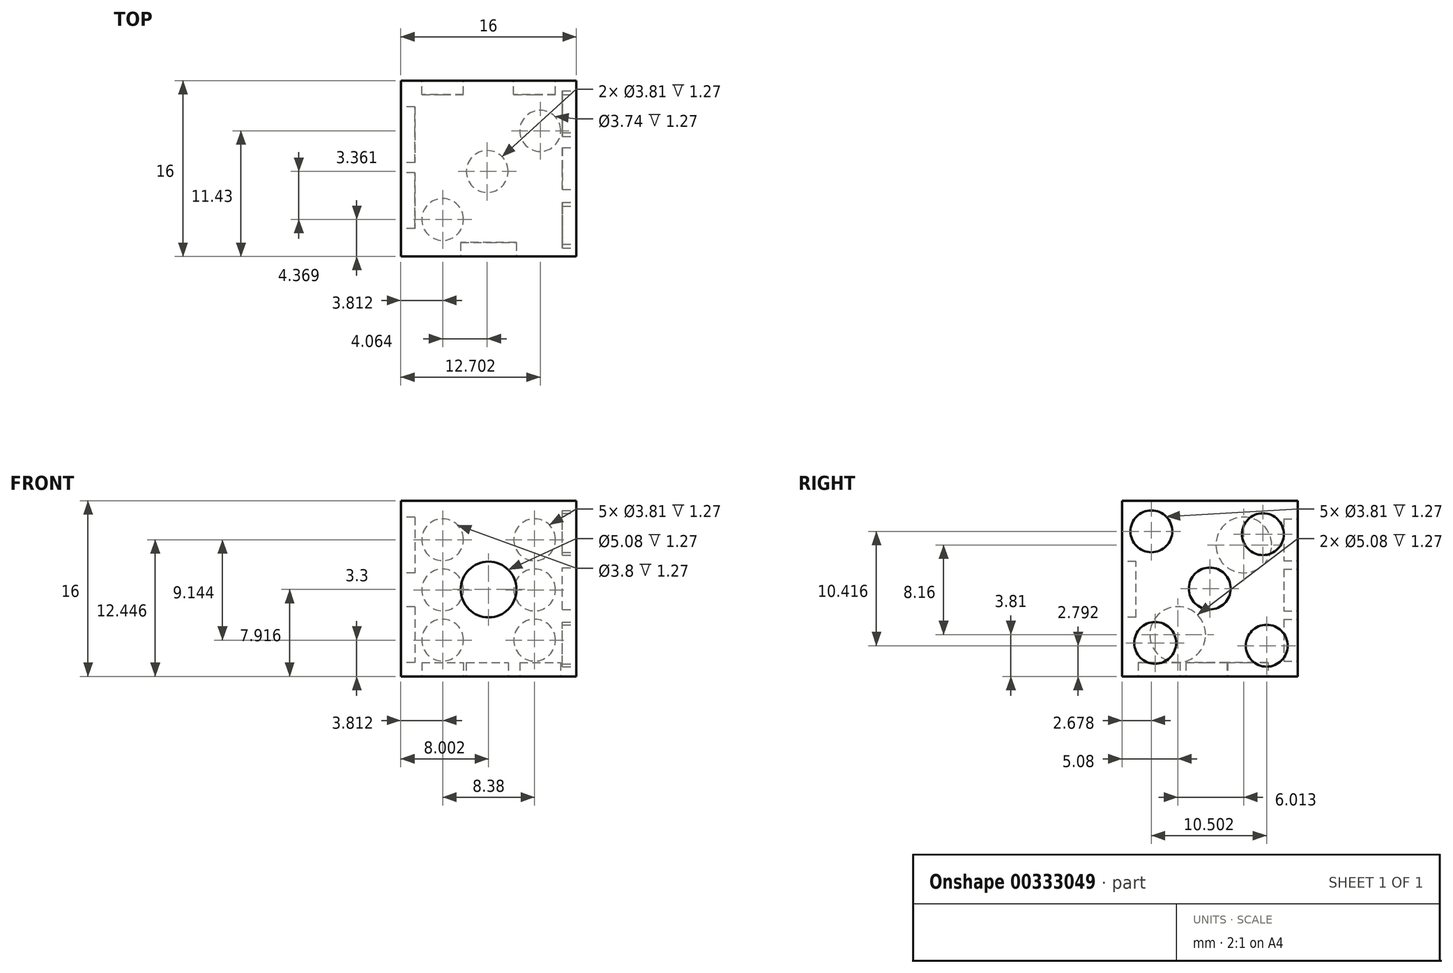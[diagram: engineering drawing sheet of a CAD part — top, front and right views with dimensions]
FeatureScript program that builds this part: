
annotation { "Feature Type Name" : "Feature", "Feature Type Description" : "" }
export const myFeature = defineFeature(function(context is Context, id is Id, definition is map)
    precondition{}
    {
        {
            var Q0;
            Q0=qCreatedBy(makeId("Front.planeOp"),FACE);
            var sketch = newSketch(context, id + "F0", { "sketchPlane" : qUnion([Q0])});
            skLineSegment(sketch, "E0.bottom", {"start": v(22.63, 56.48) * mm, "end": v(38.63, 56.48) * mm});
            skLineSegment(sketch, "E0.top", {"start": v(22.63, 40.48) * mm, "end": v(38.63, 40.48) * mm});
            skLineSegment(sketch, "E0.left", {"start": v(22.63, 56.48) * mm, "end": v(22.63, 40.48) * mm});
            skLineSegment(sketch, "E0.right", {"start": v(38.63, 56.48) * mm, "end": v(38.63, 40.48) * mm});
            skSolve(sketch);
        }
        {
            var Q0;
            Q0=makeQuery(id+"F0.imprint","IMPRINT",FACE,{"disambiguationData":[TD([[makeQuery(id+"F0.imprint","IMPRINT",EDGE,{"derivedFrom":sQuery(id+"F0.wireOp",EDGE,"E0.bottom")}),-1.0]])]});
            extrude(context, id + "F1", {"entities" : qUnion([Q0]), "oppositeDirection" : true, "depth" : 16 * mm});
        }
        {
            var Q0;
            Q0=makeQuery(id+"F1.opExtrude","CAP_FACE",FACE,{"disambiguationData":[OSD([sQuery(id+"F0.wireOp",EDGE,"E0.bottom"),sQuery(id+"F0.wireOp",EDGE,"E0.top"),sQuery(id+"F0.wireOp",EDGE,"E0.left"),sQuery(id+"F0.wireOp",EDGE,"E0.right")])],"isStart":true});
            var sketch = newSketch(context, id + "F2", { "sketchPlane" : qUnion([Q0])});
            skCircle(sketch, "E1", {"center": v(30.63, 48.4) * mm, "radius": 0.08 * mm});
            skPoint(sketch, "E1.centerSnap0", {"position": v(30.63, 40.48) * mm});
            skCircle(sketch, "E2", {"center": v(30.63, 48.4) * mm, "radius": 2.54 * mm});
            skSolve(sketch);
        }
        {
            var Q0;
            Q0=makeQuery(id+"F2.imprint","IMPRINT",FACE,{"disambiguationData":[TD([[makeQuery(id+"F2.imprint","IMPRINT",EDGE,{"derivedFrom":sQuery(id+"F2.wireOp",EDGE,"E1")}),-1.0]])]});
            extrude(context, id + "F3", {"entities" : qUnion([Q0]), "operationType" : NewBodyOperationType.REMOVE, "oppositeDirection" : true, "depth" : 1.27 * mm});
        }
        {
            var Q0;
            Q0=makeQuery(id+"F3.boolean.opBoolean","SPLIT",FACE,{"disambiguationData":[TD([makeQuery(id+"F3.opExtrude","SWEPT_FACE",FACE,{"disambiguationData":[OSD([sQuery(id+"F2.wireOp",EDGE,"E1")])]})])],"derivedFrom":makeQuery(id+"F1.opExtrude","CAP_FACE",FACE,{"disambiguationData":[OSD([sQuery(id+"F0.wireOp",EDGE,"E0.bottom"),sQuery(id+"F0.wireOp",EDGE,"E0.top"),sQuery(id+"F0.wireOp",EDGE,"E0.left"),sQuery(id+"F0.wireOp",EDGE,"E0.right")])],"isStart":true})});
            extrude(context, id + "F4", {"entities" : qUnion([Q0]), "operationType" : NewBodyOperationType.REMOVE, "oppositeDirection" : true, "depth" : 1.27 * mm});
        }
        {
            var Q0;
            Q0=makeQuery(id+"F1.opExtrude","SWEPT_FACE",FACE,{"disambiguationData":[OSD([sQuery(id+"F0.wireOp",EDGE,"E0.left")])]});
            var sketch = newSketch(context, id + "F5", { "sketchPlane" : qUnion([Q0])});
            skCircle(sketch, "E3", {"center": v(-11.1, 52.45) * mm, "radius": 2.54 * mm});
            skCircle(sketch, "E4", {"center": v(-5.08, 44.3) * mm, "radius": 2.54 * mm});
            skSolve(sketch);
        }
        {
            var Q0;
            Q0=makeQuery(id+"F5.imprint","IMPRINT",FACE,{"disambiguationData":[TD([[makeQuery(id+"F5.imprint","IMPRINT",EDGE,{"derivedFrom":sQuery(id+"F5.wireOp",EDGE,"E3")}),1.0]])]});
            extrude(context, id + "F6", {"entities" : qUnion([Q0]), "operationType" : NewBodyOperationType.REMOVE, "oppositeDirection" : true, "depth" : 1.27 * mm});
        }
        {
            var Q0;
            Q0 = qSketchRegion(id + "F5", true);
            extrude(context, id + "F7", {"entities" : qUnion([Q0]), "operationType" : NewBodyOperationType.REMOVE, "oppositeDirection" : true, "depth" : 1.27 * mm});
        }
        {
            var Q0;
            Q0=makeQuery(id+"F1.opExtrude","CAP_FACE",FACE,{"disambiguationData":[OSD([sQuery(id+"F0.wireOp",EDGE,"E0.bottom"),sQuery(id+"F0.wireOp",EDGE,"E0.top"),sQuery(id+"F0.wireOp",EDGE,"E0.left"),sQuery(id+"F0.wireOp",EDGE,"E0.right")])],"isStart":false});
            var sketch = newSketch(context, id + "F8", { "sketchPlane" : qUnion([Q0])});
            skCircle(sketch, "E5", {"center": v(-34.82, 52.92) * mm, "radius": 1.9 * mm});
            skCircle(sketch, "E6", {"center": v(-34.82, 48.35) * mm, "radius": 1.9 * mm});
            skCircle(sketch, "E7", {"center": v(-34.82, 43.78) * mm, "radius": 1.9 * mm});
            skCircle(sketch, "E8", {"center": v(-26.44, 52.93) * mm, "radius": 1.9 * mm});
            skCircle(sketch, "E9", {"center": v(-26.44, 43.78) * mm, "radius": 1.9 * mm});
            skCircle(sketch, "E10", {"center": v(-26.44, 48.35) * mm, "radius": 1.9 * mm});
            skSolve(sketch);
        }
        {
            var Q0;
            Q0 = qSketchRegion(id + "F8", true);
            extrude(context, id + "F9", {"entities" : qUnion([Q0]), "operationType" : NewBodyOperationType.REMOVE, "oppositeDirection" : true, "depth" : 1.27 * mm});
        }
        {
            var Q0;
            Q0=makeQuery(id+"F1.opExtrude","SWEPT_FACE",FACE,{"disambiguationData":[OSD([sQuery(id+"F0.wireOp",EDGE,"E0.right")])]});
            var sketch = newSketch(context, id + "F10", { "sketchPlane" : qUnion([Q0])});
            skCircle(sketch, "E11", {"center": v(8, 48.48) * mm, "radius": 1.9 * mm});
            skCircle(sketch, "E12", {"center": v(2.68, 53.69) * mm, "radius": 1.9 * mm});
            skCircle(sketch, "E13", {"center": v(12.84, 53.43) * mm, "radius": 1.9 * mm});
            skCircle(sketch, "E14", {"center": v(13.18, 43.27) * mm, "radius": 1.9 * mm});
            skCircle(sketch, "E15", {"center": v(3.02, 43.53) * mm, "radius": 1.9 * mm});
            skSolve(sketch);
        }
        {
            var Q0;
            Q0 = qSketchRegion(id + "F10", true);
            extrude(context, id + "F11", {"entities" : qUnion([Q0]), "operationType" : NewBodyOperationType.REMOVE, "oppositeDirection" : true, "depth" : 1.27 * mm});
        }
        {
            var Q0;
            Q0=makeQuery(id+"F1.opExtrude","SWEPT_FACE",FACE,{"disambiguationData":[OSD([sQuery(id+"F0.wireOp",EDGE,"E0.top")])]});
            var sketch = newSketch(context, id + "F12", { "sketchPlane" : qUnion([Q0])});
            skCircle(sketch, "E16", {"center": v(35.33, -11.43) * mm, "radius": 1.87 * mm});
            skCircle(sketch, "E17", {"center": v(30.5, -7.73) * mm, "radius": 1.9 * mm});
            skCircle(sketch, "E18", {"center": v(26.44, -3.36) * mm, "radius": 1.9 * mm});
            skSolve(sketch);
        }
        {
            var Q0;
            Q0=makeQuery(id+"F1.opExtrude","SWEPT_FACE",FACE,{"disambiguationData":[OSD([sQuery(id+"F0.wireOp",EDGE,"E0.bottom")])]});
            var sketch = newSketch(context, id + "F13", { "sketchPlane" : qUnion([Q0])});
            skSolve(sketch);
        }
        {
            var Q0;
            Q0 = qSketchRegion(id + "F12", true);
            extrude(context, id + "F14", {"entities" : qUnion([Q0]), "operationType" : NewBodyOperationType.REMOVE, "oppositeDirection" : true, "depth" : 1.27 * mm});
        }
    });
